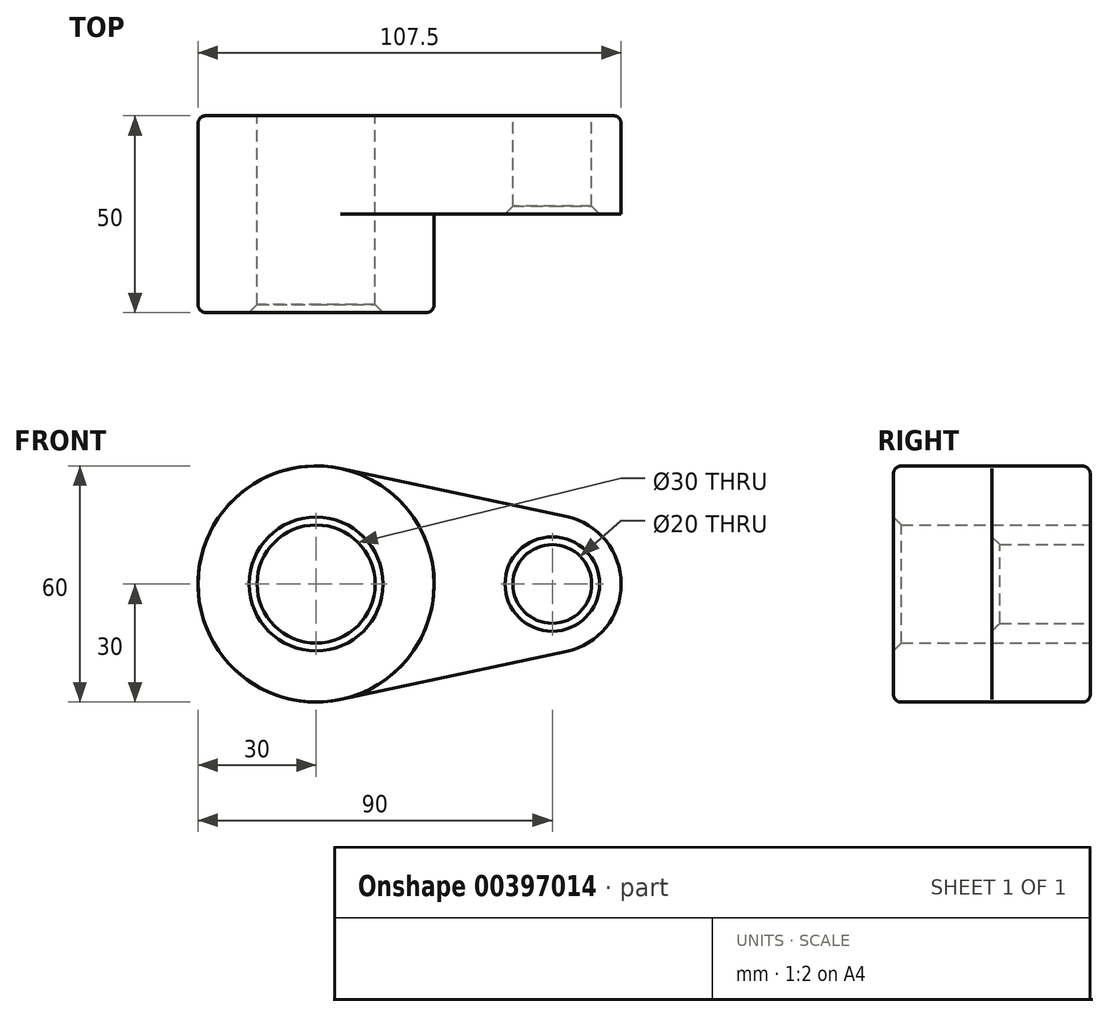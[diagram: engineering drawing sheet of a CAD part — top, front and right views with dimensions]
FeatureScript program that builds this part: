
annotation { "Feature Type Name" : "Feature", "Feature Type Description" : "" }
export const myFeature = defineFeature(function(context is Context, id is Id, definition is map)
    precondition{}
    {
        {
            var Q0;
            Q0=qCreatedBy(makeId("Front.planeOp"),FACE);
            var sketch = newSketch(context, id + "F0", { "sketchPlane" : qUnion([Q0])});
            skCircle(sketch, "E0", {"center": v(0, 0) * mm, "radius": 30 * mm});
            skCircle(sketch, "E1", {"center": v(60, 0) * mm, "radius": 17.5 * mm});
            skLineSegment(sketch, "E2", {"start": v(6.25, 29.34) * mm, "end": v(63.65, 17.12) * mm});
            skLineSegment(sketch, "E3", {"start": v(6.25, -29.34) * mm, "end": v(63.65, -17.12) * mm});
            skCircle(sketch, "E4", {"center": v(0, 0) * mm, "radius": 15 * mm});
            skCircle(sketch, "E5", {"center": v(60, 0) * mm, "radius": 10 * mm});
            skSolve(sketch);
        }
        {
            var Q0;
            Q0 = qSketchRegion(id + "F0", true);
            extrude(context, id + "F1", {"entities" : qUnion([Q0]), "depth" : 25 * mm, "offsetDistance" : 25 * mm});
        }
        {
            var Q0;
            Q0=makeQuery(id+"F0.imprint","IMPRINT",FACE,{"disambiguationData":[TD([[makeQuery(id+"F0.imprint","IMPRINT",EDGE,{"derivedFrom":sQuery(id+"F0.wireOp",EDGE,"E4")}),-1.0]])]});
            extrude(context, id + "F2", {"entities" : qUnion([Q0]), "operationType" : NewBodyOperationType.ADD, "depth" : 50 * mm, "offsetDistance" : 25 * mm});
        }
        {
            var Q0;
            Q0=makeQuery(id+"F1.opExtrude","CAP_EDGE",EDGE,{"disambiguationData":[OSD([sQuery(id+"F0.wireOp",EDGE,"E3")])],"isStart":true});
            var Q1;
            Q1=makeQuery(id+"F2.opExtrude","CAP_EDGE",EDGE,{"disambiguationData":[OSD([sQuery(id+"F0.wireOp",EDGE,"E0")])],"isStart":false});
            fillet(context, id + "F3", {"entities" : qUnion([Q0, Q1]), "radius" : 2 * mm, "tangentPropagation" : true, "allowEdgeOverflow" : false});
        }
        {
            var Q0;
            Q0=makeQuery(id+"F2.opExtrude","CAP_EDGE",EDGE,{"disambiguationData":[OSD([sQuery(id+"F0.wireOp",EDGE,"E4")])],"isStart":false});
            var Q1;
            Q1=makeQuery(id+"F1.opExtrude","CAP_EDGE",EDGE,{"disambiguationData":[OSD([sQuery(id+"F0.wireOp",EDGE,"E5")])],"isStart":false});
            chamfer(context, id + "F4", {"entities" : qUnion([Q0, Q1]), "width" : 2 * mm, "tangentPropagation" : true});
        }
    });
